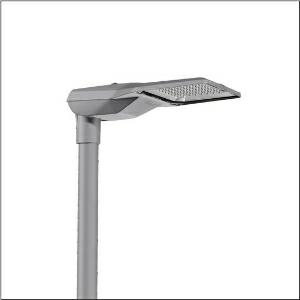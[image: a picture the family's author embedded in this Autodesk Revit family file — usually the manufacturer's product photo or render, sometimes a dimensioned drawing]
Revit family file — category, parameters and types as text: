
# Revit family: streetlight_sl_21_iq_midi___p0_5a_5xe3v31v08mb_f649
name_source: partatom
category: Lighting Fixtures
units: mm (PartAtom-declared; Revit-internal decimal feet)

## family parameters
Cut with Voids When Loaded = No
Host = Face
Light Source = No
Part Type = Normal
Room Calculation Point = No
Round Connector Dimension = Use Diameter
Shared = No

## types (1)
- --- (1 x LED, 18020 lm, 129.3 W, 3000K)
    Apparent Load = 129 VA
    CIE Flux Codes = 37 73 96 100 100
    Color Rendering = 70
    Color Temperature = 3000K
    Default Elevation = 1800 mm
    Description = Streetlight SL 21 iQ midi, mast luminaire, primary light control with lens, of PMMA, primary optical cover: cover, of toughened safety glass, transparent, light distribution: P0.5a, light emission: direct distribution, primary light characteristic: asymmetric, installation type: post-top, side-entry, LED, High Power LED, rated luminous flux: 18.020lm, luminous efficacy: 139lm/W, light colour: 730, colour temperature: 3000K, control gear: iQ-Street Remote, D4i with power reduction, control: pre-setting: logarithmic dimming characteristic, Street-Remote, Auto-Match, Temp-Guard, Lumen-Switch, Night-Set, Smart-Wire, Light-Fading, Desk-Remote (wireless, voltage-free reading and setting of iQ features in the workshop via application-optimized NFC function/RFID function), optimised constant luminous flux control (CLO 2.0), mains connection: 230..240V, AC, 50/60Hz, start of lifetime: 129W, end of service life: 142W, reduction: 56W, luminaire housing, of diecast aluminium, powder-coated, Siteco® metallic grey (DB 702S), corrosivity category C5 mid according to DIN EN ISO 12944, please order mast flange separately, inclination adjustable: 0°, 5°, 10°, 15°, sealing non-destructively replaceable, multi-level sealing system, length: 644mm, width: 335mm, height: 110mm, mast flange for spigot size: 42mm (side-entry): 5XC10008XM4, 60/48mm (side-entry/post-top): 5XC10108XM2, 76/60mm (side-entry/post-top): 5XC10108XM1, mounting height: 4..8m, Smart Interface above, protection rating (complete): IP66, insulation class (complete): insulation class II (safety insulation), certification: CE, ENEC, ENEC+, VDE, impact resistance: IK09, permissible operating ambient temperature for outdoor applications: -40..+50°C, standard-compliant lighting for roads and squares, packaging unit: 1 piece

Light Distribution: P0.5a
    Height = 111 mm
    Lamp = 1 x LED
    Lamp Light Flux = 18020 lm
    Lamp Power = 129.3 W
    Lamp count = 1
    Length = 644 mm
    Luminous efficacy = 139 lm/W
    Manufacturer = Siteco
    ModVariant = No
    Model = 5XE3V31V08MB
    Number of Poles = 1
    OnlyDefault = Yes
    Power Factor = 1
    Product Name = Streetlight SL 21 iQ midi | P0.5a
    Product group = mast luminaire | pylon top
    ProductGroupID = 6100
    Protection Class = Protection class II
    Protection Degree = IP 66
    RLX_Detail_Level = 1
    RLX_Emergency_Light_Flux = 0 lm
    RLX_Emergency_Type = 0
    RLX_Emergency_Type_DB = No
    RlxData = <blob elided: 90101 chars, md5=e3d020f8>
    Socket = socket
    Standby Power = 0 W
    System Light Flux = 18021 lm
    System Power = 129 W
    Type Comments = factory setting: luminous flux: 100 % | dim-lin: 254 | 672 mA
    Type Image = l_1004302.jpg
    URL = http://relux.com
    VarID = @adj_067410
    Voltage = 0 V
    Weight = 0.00 kg
    Width = 336 mm

## geometry (parser evidence)
native form markers: Blend x4, Sweep x10
no freeform markers — native parametric forms only
